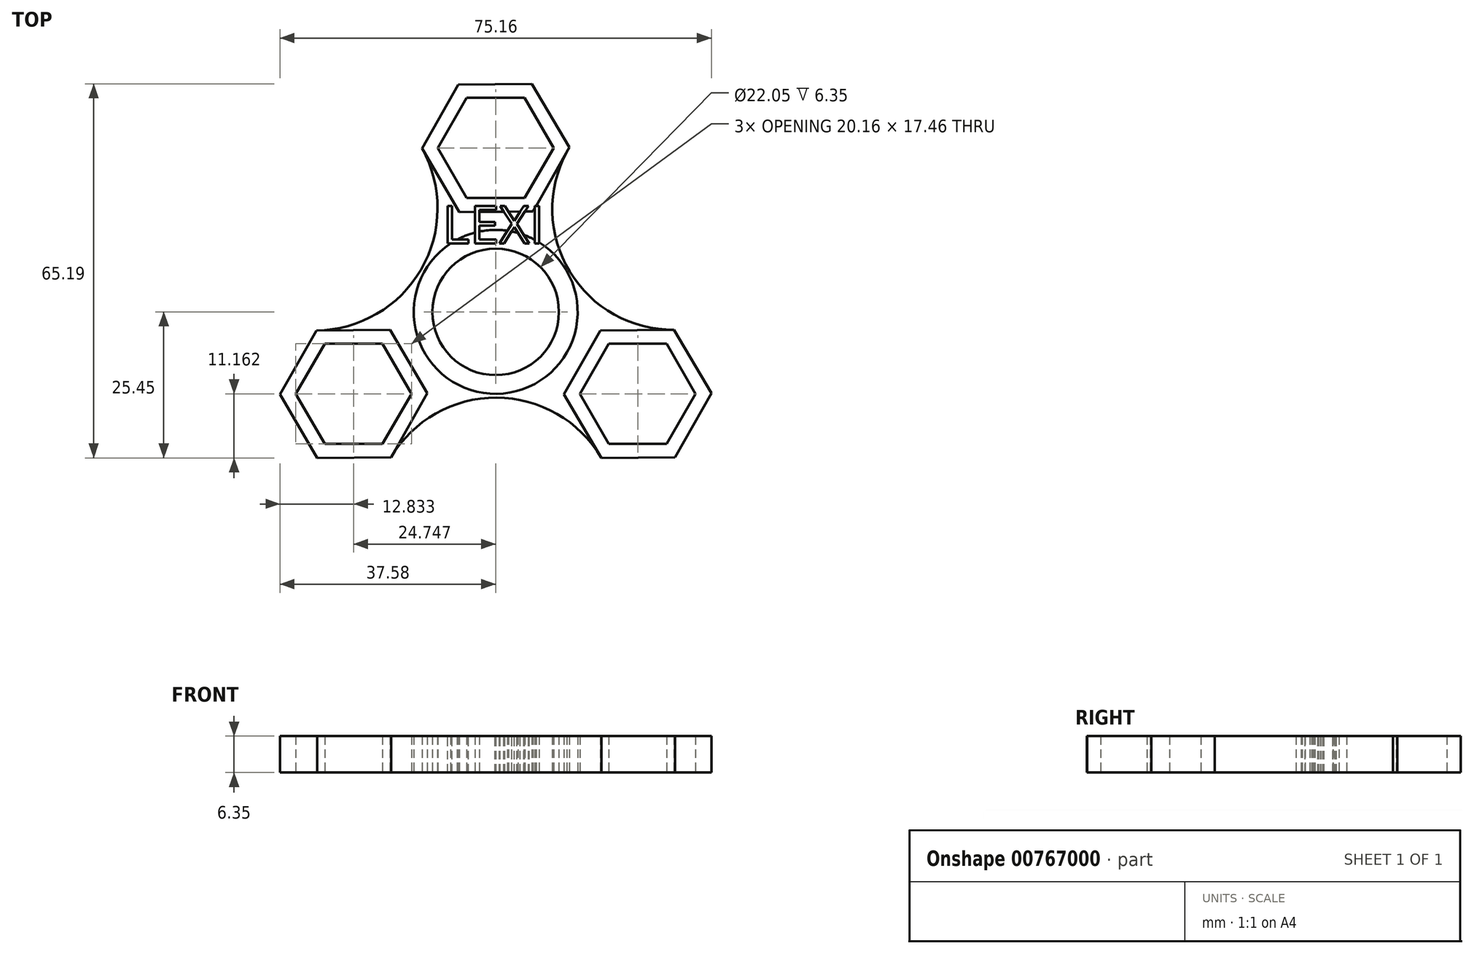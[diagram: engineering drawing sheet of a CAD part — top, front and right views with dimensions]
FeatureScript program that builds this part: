
annotation { "Feature Type Name" : "Feature", "Feature Type Description" : "" }
export const myFeature = defineFeature(function(context is Context, id is Id, definition is map)
    precondition{}
    {
        {
            var Q0;
            Q0=qCreatedBy(makeId("Top.planeOp"),FACE);
            var sketch = newSketch(context, id + "F0", { "sketchPlane" : qUnion([Q0])});
            skCircle(sketch, "E0", {"center": v(0, 0) * mm, "radius": 11.02 * mm});
            skCircle(sketch, "E1", {"center": v(0, 0) * mm, "radius": 14.29 * mm});
            skCircle(sketch, "E2.cCircle", {"center": v(0, 28.58) * mm, "radius": 8.73 * mm, "construction": true});
            skLineSegment(sketch, "E2.0", {"start": v(-5.04, 37.3) * mm, "end": v(5.04, 37.3) * mm});
            skLineSegment(sketch, "E2.1", {"start": v(5.04, 37.3) * mm, "end": v(10.08, 28.58) * mm});
            skLineSegment(sketch, "E2.2", {"start": v(10.08, 28.58) * mm, "end": v(5.04, 19.84) * mm});
            skLineSegment(sketch, "E2.3", {"start": v(5.04, 19.84) * mm, "end": v(-5.04, 19.84) * mm});
            skLineSegment(sketch, "E2.4", {"start": v(-5.04, 19.84) * mm, "end": v(-10.08, 28.57) * mm});
            skLineSegment(sketch, "E2.5", {"start": v(-10.08, 28.57) * mm, "end": v(-5.04, 37.3) * mm});
            skPoint(sketch, "E2.0.midPoint", {"position": v(0, 37.3) * mm});
            skCircle(sketch, "E3.cCircle", {"center": v(0, 28.58) * mm, "radius": 11.11 * mm, "construction": true});
            skLineSegment(sketch, "E3.0", {"start": v(6.33, 39.74) * mm, "end": v(12.83, 28.68) * mm});
            skLineSegment(sketch, "E3.1", {"start": v(12.83, 28.68) * mm, "end": v(6.5, 17.51) * mm});
            skLineSegment(sketch, "E3.2", {"start": v(6.5, 17.51) * mm, "end": v(-6.33, 17.41) * mm});
            skLineSegment(sketch, "E3.3", {"start": v(-6.33, 17.41) * mm, "end": v(-12.83, 28.47) * mm});
            skLineSegment(sketch, "E3.4", {"start": v(-12.83, 28.47) * mm, "end": v(-6.5, 39.64) * mm});
            skLineSegment(sketch, "E3.5", {"start": v(-6.5, 39.64) * mm, "end": v(6.33, 39.74) * mm});
            skPoint(sketch, "E3.0.midPoint", {"position": v(9.58, 34.2) * mm});
            skPoint(sketch, "E4.1.0", {"position": v(-32.3, -18.65) * mm});
            skCircle(sketch, "E4.1.1", {"center": v(-24.75, -14.29) * mm, "radius": 8.73 * mm, "construction": true});
            skPoint(sketch, "E4.1.2", {"position": v(-34.42, -8.8) * mm});
            skLineSegment(sketch, "E4.1.3", {"start": v(-18.24, -25.35) * mm, "end": v(-31.07, -25.45) * mm});
            skCircle(sketch, "E4.1.4", {"center": v(-24.75, -14.29) * mm, "radius": 11.11 * mm, "construction": true});
            skLineSegment(sketch, "E4.1.5", {"start": v(-18.42, -3.12) * mm, "end": v(-11.92, -14.18) * mm});
            skLineSegment(sketch, "E4.1.6", {"start": v(-31.07, -25.45) * mm, "end": v(-37.58, -14.4) * mm});
            skLineSegment(sketch, "E4.1.7", {"start": v(-31.25, -3.23) * mm, "end": v(-18.42, -3.12) * mm});
            skLineSegment(sketch, "E4.1.8", {"start": v(-37.58, -14.4) * mm, "end": v(-31.25, -3.23) * mm});
            skLineSegment(sketch, "E4.1.9", {"start": v(-19.7, -23.02) * mm, "end": v(-29.79, -23.02) * mm});
            skLineSegment(sketch, "E4.1.10", {"start": v(-14.66, -14.29) * mm, "end": v(-19.7, -23.02) * mm});
            skLineSegment(sketch, "E4.1.11", {"start": v(-11.92, -14.18) * mm, "end": v(-18.24, -25.35) * mm});
            skLineSegment(sketch, "E4.1.12", {"start": v(-19.7, -5.56) * mm, "end": v(-14.66, -14.29) * mm});
            skLineSegment(sketch, "E4.1.13", {"start": v(-29.79, -5.56) * mm, "end": v(-19.7, -5.56) * mm});
            skLineSegment(sketch, "E4.1.14", {"start": v(-34.83, -14.29) * mm, "end": v(-29.79, -5.56) * mm});
            skLineSegment(sketch, "E4.1.15", {"start": v(-29.79, -23.02) * mm, "end": v(-34.83, -14.29) * mm});
            skPoint(sketch, "E4.2.0", {"position": v(32.3, -18.65) * mm});
            skCircle(sketch, "E4.2.1", {"center": v(24.75, -14.29) * mm, "radius": 8.73 * mm, "construction": true});
            skPoint(sketch, "E4.2.2", {"position": v(24.84, -25.4) * mm});
            skLineSegment(sketch, "E4.2.3", {"start": v(31.07, -3.12) * mm, "end": v(37.58, -14.18) * mm});
            skCircle(sketch, "E4.2.4", {"center": v(24.75, -14.29) * mm, "radius": 11.11 * mm, "construction": true});
            skLineSegment(sketch, "E4.2.5", {"start": v(11.92, -14.4) * mm, "end": v(18.24, -3.23) * mm});
            skLineSegment(sketch, "E4.2.6", {"start": v(37.58, -14.18) * mm, "end": v(31.25, -25.35) * mm});
            skLineSegment(sketch, "E4.2.7", {"start": v(18.42, -25.45) * mm, "end": v(11.92, -14.4) * mm});
            skLineSegment(sketch, "E4.2.8", {"start": v(31.25, -25.35) * mm, "end": v(18.42, -25.45) * mm});
            skLineSegment(sketch, "E4.2.9", {"start": v(29.79, -5.56) * mm, "end": v(34.83, -14.29) * mm});
            skLineSegment(sketch, "E4.2.10", {"start": v(19.7, -5.56) * mm, "end": v(29.79, -5.56) * mm});
            skLineSegment(sketch, "E4.2.11", {"start": v(18.24, -3.23) * mm, "end": v(31.07, -3.12) * mm});
            skLineSegment(sketch, "E4.2.12", {"start": v(14.66, -14.29) * mm, "end": v(19.7, -5.56) * mm});
            skLineSegment(sketch, "E4.2.13", {"start": v(19.7, -23.02) * mm, "end": v(14.66, -14.29) * mm});
            skLineSegment(sketch, "E4.2.14", {"start": v(29.79, -23.02) * mm, "end": v(19.7, -23.02) * mm});
            skLineSegment(sketch, "E4.2.15", {"start": v(34.83, -14.29) * mm, "end": v(29.79, -23.02) * mm});
            skSolve(sketch);
        }
        {
            var Q0;
            Q0=qCreatedBy(makeId("Top.planeOp"),FACE);
            var sketch = newSketch(context, id + "F1", { "sketchPlane" : qUnion([Q0])});
            skLineSegment(sketch, "E5.0", {"start": v(18.24, -3.23) * mm, "end": v(31.07, -3.12) * mm});
            skLineSegment(sketch, "E5.1", {"start": v(-19.7, -23.02) * mm, "end": v(-29.79, -23.02) * mm});
            skLineSegment(sketch, "E5.2", {"start": v(-18.42, -3.12) * mm, "end": v(-11.92, -14.18) * mm});
            skLineSegment(sketch, "E5.3", {"start": v(5.04, 37.3) * mm, "end": v(10.08, 28.58) * mm});
            skLineSegment(sketch, "E5.4", {"start": v(10.08, 28.58) * mm, "end": v(5.04, 19.84) * mm});
            skLineSegment(sketch, "E5.5", {"start": v(5.04, 19.84) * mm, "end": v(-5.04, 19.84) * mm});
            skLineSegment(sketch, "E5.6", {"start": v(-29.79, -5.56) * mm, "end": v(-19.7, -5.56) * mm});
            skLineSegment(sketch, "E5.7", {"start": v(18.42, -25.45) * mm, "end": v(11.92, -14.4) * mm});
            skLineSegment(sketch, "E5.8", {"start": v(-6.33, 17.41) * mm, "end": v(-12.83, 28.47) * mm});
            skLineSegment(sketch, "E5.9", {"start": v(6.5, 17.51) * mm, "end": v(-6.33, 17.41) * mm});
            skLineSegment(sketch, "E5.10", {"start": v(-12.83, 28.47) * mm, "end": v(-6.5, 39.64) * mm});
            skLineSegment(sketch, "E5.11", {"start": v(12.83, 28.68) * mm, "end": v(6.5, 17.51) * mm});
            skLineSegment(sketch, "E5.12", {"start": v(-6.5, 39.64) * mm, "end": v(6.33, 39.74) * mm});
            skCircle(sketch, "E5.13", {"center": v(0, 0) * mm, "radius": 11.02 * mm});
            skLineSegment(sketch, "E5.15", {"start": v(-10.08, 28.57) * mm, "end": v(-5.04, 37.3) * mm});
            skLineSegment(sketch, "E5.16", {"start": v(-19.7, -5.56) * mm, "end": v(-14.66, -14.29) * mm});
            skCircle(sketch, "E5.17", {"center": v(0, 0) * mm, "radius": 14.29 * mm});
            skLineSegment(sketch, "E5.18", {"start": v(-5.04, 19.84) * mm, "end": v(-10.08, 28.57) * mm});
            skCircle(sketch, "E5.19", {"center": v(0, 28.58) * mm, "radius": 8.73 * mm});
            skLineSegment(sketch, "E5.20", {"start": v(-31.07, -25.45) * mm, "end": v(-37.58, -14.4) * mm});
            skLineSegment(sketch, "E5.21", {"start": v(31.25, -25.35) * mm, "end": v(18.42, -25.45) * mm});
            skCircle(sketch, "E5.22", {"center": v(-24.75, -14.29) * mm, "radius": 8.73 * mm});
            skLineSegment(sketch, "E5.24", {"start": v(-34.83, -14.29) * mm, "end": v(-29.79, -5.56) * mm});
            skLineSegment(sketch, "E5.25", {"start": v(14.66, -14.29) * mm, "end": v(19.7, -5.56) * mm});
            skLineSegment(sketch, "E5.26", {"start": v(-14.66, -14.29) * mm, "end": v(-19.7, -23.02) * mm});
            skLineSegment(sketch, "E5.27", {"start": v(-31.25, -3.23) * mm, "end": v(-18.42, -3.12) * mm});
            skCircle(sketch, "E5.28", {"center": v(24.75, -14.29) * mm, "radius": 8.73 * mm});
            skLineSegment(sketch, "E5.29", {"start": v(29.79, -5.56) * mm, "end": v(34.83, -14.29) * mm});
            skLineSegment(sketch, "E5.30", {"start": v(-18.24, -25.35) * mm, "end": v(-31.07, -25.45) * mm});
            skLineSegment(sketch, "E5.31", {"start": v(11.92, -14.4) * mm, "end": v(18.24, -3.23) * mm});
            skLineSegment(sketch, "E5.32", {"start": v(19.7, -23.02) * mm, "end": v(14.66, -14.29) * mm});
            skLineSegment(sketch, "E5.33", {"start": v(-11.92, -14.18) * mm, "end": v(-18.24, -25.35) * mm});
            skLineSegment(sketch, "E5.34", {"start": v(31.07, -3.12) * mm, "end": v(37.58, -14.18) * mm});
            skLineSegment(sketch, "E5.35", {"start": v(19.7, -5.56) * mm, "end": v(29.79, -5.56) * mm});
            skLineSegment(sketch, "E5.37", {"start": v(37.58, -14.18) * mm, "end": v(31.25, -25.35) * mm});
            skLineSegment(sketch, "E5.38", {"start": v(6.33, 39.74) * mm, "end": v(12.83, 28.68) * mm});
            skLineSegment(sketch, "E5.39", {"start": v(29.79, -23.02) * mm, "end": v(19.7, -23.02) * mm});
            skArc(sketch, "E6", {"start": v(-31.25, -3.23) * mm, "mid": v(-13, 7.37) * mm, "end": v(-12.83, 28.47) * mm});
            skArc(sketch, "E7", {"start": v(18.42, -25.45) * mm, "mid": v(0.12, -14.95) * mm, "end": v(-18.24, -25.35) * mm});
            skArc(sketch, "E8", {"start": v(12.83, 28.68) * mm, "mid": v(12.65, 7.45) * mm, "end": v(31.07, -3.12) * mm});
            skLineSegment(sketch, "E9", {"start": v(-5.04, 37.3) * mm, "end": v(5.04, 37.3) * mm});
            skLineSegment(sketch, "E10", {"start": v(34.83, -14.29) * mm, "end": v(29.79, -23.02) * mm});
            skLineSegment(sketch, "E11", {"start": v(-34.83, -14.29) * mm, "end": v(-29.79, -23.02) * mm});
            skLineSegment(sketch, "E12", {"start": v(-31.25, -3.23) * mm, "end": v(-37.58, -14.4) * mm});
            skSolve(sketch);
        }
        {
            var Q0;
            Q0=makeQuery(id+"F1.imprint","IMPRINT",FACE,{"disambiguationData":[TD([[makeQuery(id+"F1.imprint","IMPRINT",EDGE,{"derivedFrom":sQuery(id+"F1.wireOp",EDGE,"E5.17")}),-1.0]])]});
            var Q1;
            Q1=makeQuery(id+"F0.imprint","IMPRINT",FACE,{"disambiguationData":[TD([[makeQuery(id+"F0.imprint","IMPRINT",EDGE,{"derivedFrom":sQuery(id+"F0.wireOp",EDGE,"E0")}),-1.0]])]});
            var Q2;
            Q2=makeQuery(id+"F0.imprint","IMPRINT",FACE,{"disambiguationData":[TD([[makeQuery(id+"F0.imprint","IMPRINT",EDGE,{"derivedFrom":sQuery(id+"F0.wireOp",EDGE,"E2.0")}),1.0]])]});
            var Q3;
            {var subQ11=sQuery(id+"F1.wireOp",EDGE,"E5.23");var subQ12=makeQuery(id+"F1.imprint","INTERSECT",VERTEX,{"derivedFrom":[sQuery(id+"F1.wireOp",EDGE,"E5.21"),subQ11]});Q3=makeQuery(id+"F1.imprint","IMPRINT",FACE,{"disambiguationData":[TD([[makeQuery(id+"F1.imprint","IMPRINT",EDGE,{"disambiguationData":[TD([[subQ12,-1.0]])],"derivedFrom":subQ11}),1.0]])]});}
            var Q4;
            Q4=makeQuery(id+"F0.imprint","IMPRINT",FACE,{"disambiguationData":[TD([[makeQuery(id+"F0.imprint","IMPRINT",EDGE,{"derivedFrom":sQuery(id+"F0.wireOp",EDGE,"E4.1.3")}),-1.0]])]});
            var Q5;
            Q5=makeQuery(id+"F0.imprint","IMPRINT",FACE,{"disambiguationData":[TD([[makeQuery(id+"F0.imprint","IMPRINT",EDGE,{"derivedFrom":sQuery(id+"F0.wireOp",EDGE,"E4.2.3")}),-1.0]])]});
            extrude(context, id + "F2", {"entities" : qUnion([Q0, Q1, Q2, Q3, Q4, Q5]), "depth" : 6.35 * mm, "offsetDistance" : 25.4 * mm});
        }
        {
            var Q0;
            Q0=makeQuery(id+"F2.opExtrude","CAP_FACE",FACE,{"disambiguationData":[OSD([sQuery(id+"F1.wireOp",EDGE,"E5.0"),sQuery(id+"F1.wireOp",EDGE,"E5.2"),sQuery(id+"F1.wireOp",EDGE,"E5.7"),sQuery(id+"F1.wireOp",EDGE,"E5.8"),sQuery(id+"F1.wireOp",EDGE,"E5.9"),sQuery(id+"F1.wireOp",EDGE,"E5.11"),sQuery(id+"F1.wireOp",EDGE,"E5.17"),sQuery(id+"F1.wireOp",EDGE,"E5.27"),sQuery(id+"F1.wireOp",EDGE,"E5.31"),sQuery(id+"F1.wireOp",EDGE,"E5.33"),sQuery(id+"F1.wireOp",EDGE,"E6"),sQuery(id+"F1.wireOp",EDGE,"E7"),sQuery(id+"F1.wireOp",EDGE,"E8")])],"isStart":false});
            var sketch = newSketch(context, id + "F3", { "sketchPlane" : qUnion([Q0])});
            skText(sketch, "E13", { "text": "LEXI", "fontName": "OpenSans-Regular.ttf"});
            const initialGuessF3  = {"E13": [-0.00927, 0.01192, 1, 0, 0.00661]};
            skSetInitialGuess(sketch, initialGuessF3);
            skSolve(sketch);
        }
        {
            var Q0;
            Q0 = qSketchRegion(id + "F3", true);
            extrude(context, id + "F4", {"entities" : qUnion([Q0]), "operationType" : NewBodyOperationType.REMOVE, "oppositeDirection" : true, "depth" : 25.4 * mm, "offsetDistance" : 25.4 * mm});
        }
    });
